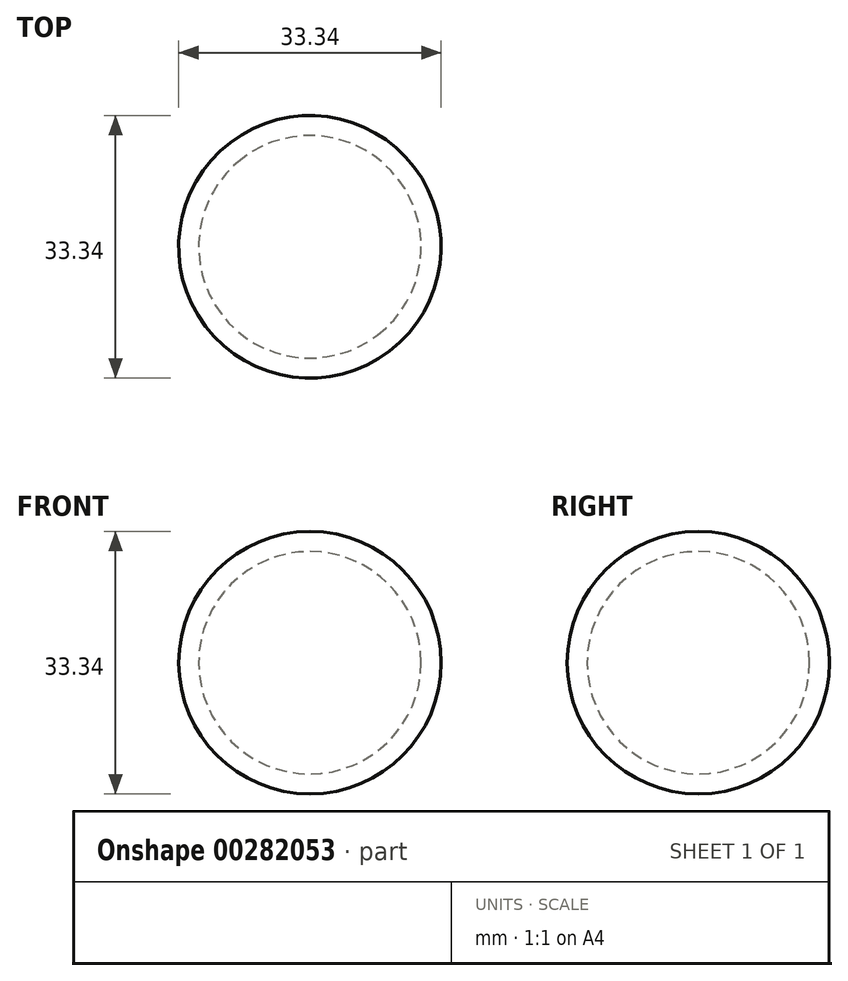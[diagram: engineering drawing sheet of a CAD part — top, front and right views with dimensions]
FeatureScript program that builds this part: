
annotation { "Feature Type Name" : "Feature", "Feature Type Description" : "" }
export const myFeature = defineFeature(function(context is Context, id is Id, definition is map)
    precondition{}
    {
        {
            var Q0;
            Q0=qCreatedBy(makeId("Top.planeOp"),FACE);
            var sketch = newSketch(context, id + "F0", { "sketchPlane" : qUnion([Q0])});
            skArc(sketch, "E0", {"start": v(8.57, -11.23) * mm, "mid": v(11.23, 8.57) * mm, "end": v(-8.57, 11.23) * mm});
            skArc(sketch, "E1", {"start": v(10.1, -13.25) * mm, "mid": v(13.25, 10.1) * mm, "end": v(-10.1, 13.25) * mm});
            skLineSegment(sketch, "E2", {"start": v(-8.57, 11.23) * mm, "end": v(-10.1, 13.25) * mm});
            skLineSegment(sketch, "E3", {"start": v(8.57, -11.23) * mm, "end": v(10.1, -13.25) * mm});
            skSolve(sketch);
        }
        {
            var Q0;
            Q0=makeQuery(id+"F0.imprint","IMPRINT",FACE,{"disambiguationData":[TD([[makeQuery(id+"F0.imprint","IMPRINT",EDGE,{"derivedFrom":sQuery(id+"F0.wireOp",EDGE,"E0")}),-1.0]])]});
            var Q1;
            Q1=sQuery(id+"F0.wireOp",EDGE,"E2");
            revolve(context, id + "F1", {"entities" : qUnion([Q0]), "axis" : qUnion([Q1]), "revolveType" : RevolveType.FULL});
        }
    });
